# Revit family: 15.Вытяжной крышный вентилятор KW
name_source: partatom
category: Оборудование
revit_build: Autodesk Revit 2016 (Build: 20151209_0715(x64)
units: mm (PartAtom-declared; Revit-internal decimal feet)

## family parameters
Всегда вертикально = Да
На основе рабочей плоскости = Нет
Общий = Нет
При загрузке вырезать с полостями = Нет
Размер круглого соединителя = Использовать диаметр
Тип детали = Нормальный
Точка расчета площади = Нет

## types (14) — shared parameters
Единица измерения = шт.
Завод изготовитель = KORF
Ключевая пометка = Вентиляция
Материал = Сталь серая
Наименование и тех.хар-ка = Вытяжной крышный вентилятор
Раздел = ОВ

## per-type parameters (varying)
| type | h | А | А1 | Б | Б1 | Высота | Масса единицы | Мощность, кВт | Напряжение U,В | Сила тока J, А | Тип, марка, обозначение | Частота вращения n, об/мин | Ширина | отступ |
| 30/22-2E | 30 мм | 300 мм | 385 мм | 252 мм | 176 мм | 300 мм | 6.4 кг | 0 Вт | 1-220 | 0.71 | KW 30/22-2E | 2770 | 300 мм | 30 мм |
| 40/31-4D | 40 мм | 400 мм | 580 мм | 350 мм | 245 мм | 400 мм | 15 кг | 0 Вт | 3-380/3-220 | 0.39/0.68 | KW 40/31-4D | 1360 | 400 мм | 40 мм |
| 40/32-4D | 40 мм | 400 мм | 580 мм | 350 мм | 245 мм | 400 мм | 17.4 кг | 0 Вт | 3-380/3-220 | 0.35/0.6 | KW 40/32-4D | 1390 | 400 мм | 40 мм |
| 56/35-4E | 40 мм | 560 мм | 780 мм | 425 мм | 298 мм | 560 мм | 29.6 кг | 0 Вт | 1-220 | 1.45 | KW 56/35-4E | 1360 | 560 мм | 56 мм |
| 56/35-4D | 40 мм | 560 мм | 780 мм | 425 мм | 298 мм | 560 мм | 30.4 кг | 0 Вт | 3-380/3-220 | 0.5/0.86 | KW 56/35-4D | 1330 | 560 мм | 56 мм |
| 56/40-4E | 40 мм | 560 мм | 780 мм | 425 мм | 298 мм | 560 мм | 29.8 кг | 1 Вт | 1-220 | 2.5 | KW 56/40-4E | 1340 | 560 мм | 56 мм |
| 56/40-4D | 40 мм | 560 мм | 780 мм | 425 мм | 298 мм | 560 мм | 30.8 кг | 1 Вт | 3-380/3-220 | 1.1/1.9 | KW 56/40-4D | 1350 | 560 мм | 56 мм |
| 63/45-4E | 40 мм | 630 мм | 870 мм | 455 мм | 319 мм | 630 мм | 40.5 кг | 1 Вт | 1-220 | 4.1 | KW 63/45-4E | 1230 | 630 мм | 63 мм |
| 63/45-4D | 40 мм | 630 мм | 870 мм | 455 мм | 319 мм | 630 мм | 40 кг | 1 Вт | 3-380/3-220 | 1.45/2.51 | KW 63/45-4D | 1220 | 630 мм | 63 мм |
| 63/50-4D | 40 мм | 630 мм | 870 мм | 455 мм | 319 мм | 630 мм | 48.4 кг | 2 Вт | 3-380/3-220 | 3/5.2 | KW 63/50-4D | 1340 | 630 мм | 63 мм |
| 63/50-6D | 40 мм | 630 мм | 870 мм | 455 мм | 319 мм | 630 мм | 40.7 кг | 1 Вт | 3-380/3-220 | 1.45/2.51 | KW 63/50-6D | 850 | 630 мм | 63 мм |
| 90/56-4D | 40 мм | 900 мм | 1250 мм | 630 мм | 441 мм | 900 мм | 77 кг | 2 Вт | 3-380/3-220 | 3.8/6.58 | KW 90/56-4D | 1370 | 900 мм | 90 мм |
| 90/56-6D | 40 мм | 900 мм | 1250 мм | 630 мм | 441 мм | 900 мм | 70 кг | 1 Вт | 3-380/3-220 | 1.55/2.68 | KW 90/56-6D | 830 | 900 мм | 90 мм |
| 90/63-6D | 40 мм | 900 мм | 1250 мм | 630 мм | 441 мм | 900 мм | 78 кг | 1 Вт | 3-380/3-220 | 2.73/4.73 | KW 90/63-6D | 870 | 900 мм | 90 мм |
